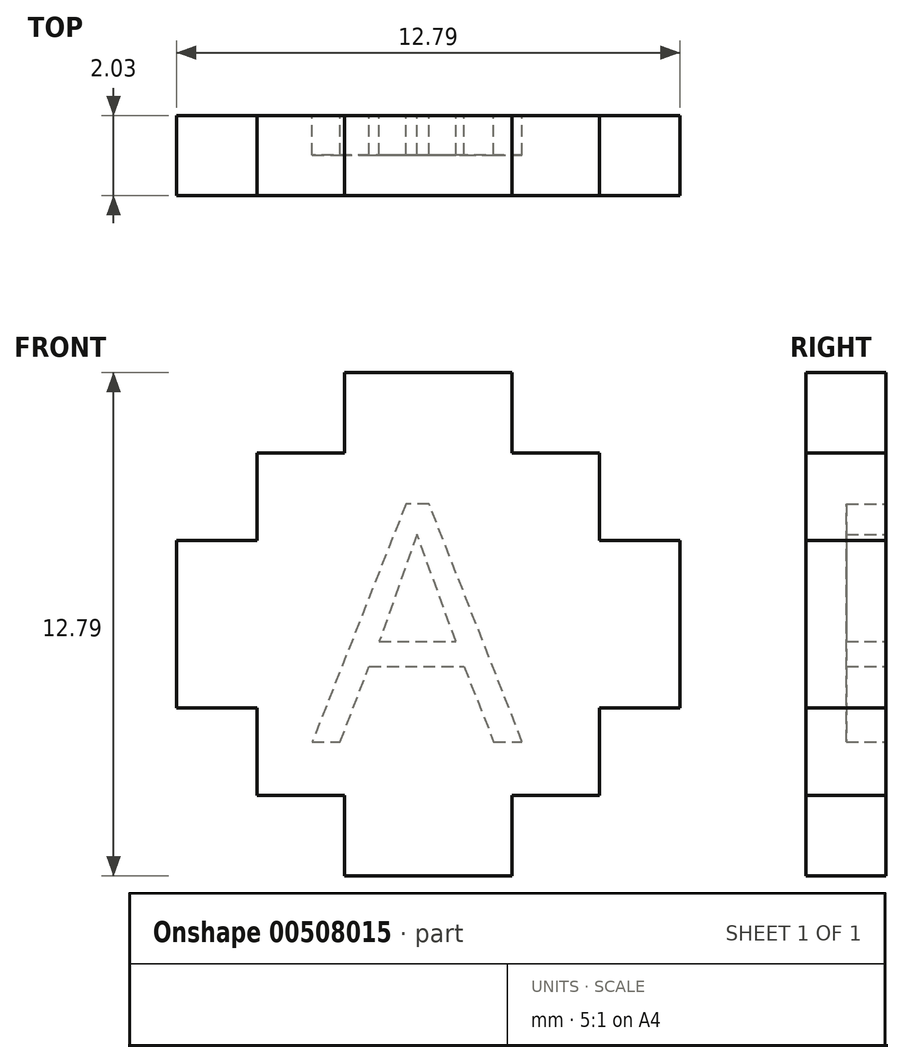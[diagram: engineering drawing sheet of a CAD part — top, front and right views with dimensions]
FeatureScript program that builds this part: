
annotation { "Feature Type Name" : "Feature", "Feature Type Description" : "" }
export const myFeature = defineFeature(function(context is Context, id is Id, definition is map)
    precondition{}
    {
        {
            var Q0;
            Q0=qCreatedBy(makeId("Front.planeOp"),FACE);
            var sketch = newSketch(context, id + "F0", { "sketchPlane" : qUnion([Q0])});
            skLineSegment(sketch, "E0", {"start": v(-17.35, 36.23) * mm, "end": v(-15.22, 36.23) * mm});
            skLineSegment(sketch, "E1", {"start": v(-15.22, 36.23) * mm, "end": v(-15.22, 34.18) * mm});
            skLineSegment(sketch, "E2", {"start": v(-15.22, 34.18) * mm, "end": v(-13, 34.18) * mm});
            skLineSegment(sketch, "E3", {"start": v(-13, 34.18) * mm, "end": v(-13, 31.96) * mm});
            skLineSegment(sketch, "E4", {"start": v(-13, 31.96) * mm, "end": v(-10.95, 31.96) * mm});
            skLineSegment(sketch, "E5", {"start": v(-10.95, 31.96) * mm, "end": v(-10.95, 29.83) * mm});
            skLineSegment(sketch, "E6", {"start": v(-17.35, 36.23) * mm, "end": v(-17.35, 28.94) * mm, "construction": true});
            skLineSegment(sketch, "E7.MirrorCS", {"start": v(-17.35, 36.23) * mm, "end": v(-19.48, 36.23) * mm});
            skLineSegment(sketch, "E8.MirrorCS", {"start": v(-19.48, 36.23) * mm, "end": v(-19.48, 34.18) * mm});
            skLineSegment(sketch, "E9.MirrorCS", {"start": v(-19.48, 34.18) * mm, "end": v(-21.7, 34.18) * mm});
            skLineSegment(sketch, "E10.MirrorCS", {"start": v(-21.7, 34.18) * mm, "end": v(-21.7, 31.96) * mm});
            skLineSegment(sketch, "E11.MirrorCS", {"start": v(-21.7, 31.96) * mm, "end": v(-23.74, 31.96) * mm});
            skLineSegment(sketch, "E12.MirrorCS", {"start": v(-23.74, 31.96) * mm, "end": v(-23.74, 29.83) * mm});
            skLineSegment(sketch, "E13", {"start": v(-23.74, 29.83) * mm, "end": v(-10.95, 29.83) * mm, "construction": true});
            skLineSegment(sketch, "E14.MirrorCS", {"start": v(-23.74, 27.7) * mm, "end": v(-23.74, 29.83) * mm});
            skLineSegment(sketch, "E15.MirrorCS", {"start": v(-21.7, 27.7) * mm, "end": v(-23.74, 27.7) * mm});
            skLineSegment(sketch, "E16.MirrorCS", {"start": v(-21.7, 25.48) * mm, "end": v(-21.7, 27.7) * mm});
            skLineSegment(sketch, "E17.MirrorCS", {"start": v(-19.48, 25.48) * mm, "end": v(-21.7, 25.48) * mm});
            skLineSegment(sketch, "E18.MirrorCS", {"start": v(-19.48, 23.44) * mm, "end": v(-19.48, 25.48) * mm});
            skLineSegment(sketch, "E19.MirrorCS", {"start": v(-17.35, 23.44) * mm, "end": v(-19.48, 23.44) * mm});
            skLineSegment(sketch, "E20.MirrorCS", {"start": v(-17.35, 23.44) * mm, "end": v(-15.22, 23.44) * mm});
            skLineSegment(sketch, "E21.MirrorCS", {"start": v(-15.22, 23.44) * mm, "end": v(-15.22, 25.48) * mm});
            skLineSegment(sketch, "E22.MirrorCS", {"start": v(-15.22, 25.48) * mm, "end": v(-13, 25.48) * mm});
            skLineSegment(sketch, "E23.MirrorCS", {"start": v(-13, 25.48) * mm, "end": v(-13, 27.7) * mm});
            skLineSegment(sketch, "E24.MirrorCS", {"start": v(-13, 27.7) * mm, "end": v(-10.95, 27.7) * mm});
            skLineSegment(sketch, "E25.MirrorCS", {"start": v(-10.95, 27.7) * mm, "end": v(-10.95, 29.83) * mm});
            skLineSegment(sketch, "E26", {"start": v(-17.63, 32.12) * mm, "end": v(-18.6, 29.4) * mm});
            skLineSegment(sketch, "E27", {"start": v(-18.6, 29.4) * mm, "end": v(-16.64, 29.4) * mm});
            skLineSegment(sketch, "E28", {"start": v(-16.64, 29.4) * mm, "end": v(-17.63, 32.12) * mm});
            skLineSegment(sketch, "E29", {"start": v(-17.91, 32.9) * mm, "end": v(-20.29, 26.85) * mm});
            skLineSegment(sketch, "E30", {"start": v(-20.29, 26.85) * mm, "end": v(-19.58, 26.85) * mm});
            skLineSegment(sketch, "E31", {"start": v(-19.58, 26.85) * mm, "end": v(-18.85, 28.76) * mm});
            skLineSegment(sketch, "E32", {"start": v(-18.85, 28.76) * mm, "end": v(-16.43, 28.76) * mm});
            skLineSegment(sketch, "E33", {"start": v(-16.43, 28.76) * mm, "end": v(-15.68, 26.85) * mm});
            skLineSegment(sketch, "E34", {"start": v(-15.68, 26.85) * mm, "end": v(-14.96, 26.85) * mm});
            skLineSegment(sketch, "E35", {"start": v(-14.96, 26.85) * mm, "end": v(-17.32, 32.89) * mm});
            skLineSegment(sketch, "E36", {"start": v(-17.32, 32.89) * mm, "end": v(-17.91, 32.9) * mm});
            skSolve(sketch);
        }
        {
            var Q0;
            Q0=makeQuery(id+"F0.imprint","IMPRINT",FACE,{"disambiguationData":[TD([[makeQuery(id+"F0.imprint","IMPRINT",EDGE,{"derivedFrom":sQuery(id+"F0.wireOp",EDGE,"E0")}),-1.0]])]});
            var Q1;
            Q1=makeQuery(id+"F0.imprint","IMPRINT",FACE,{"disambiguationData":[TD([[makeQuery(id+"F0.imprint","IMPRINT",EDGE,{"derivedFrom":sQuery(id+"F0.wireOp",EDGE,"b25c118d-44e0-46fb-885b-121db1910a24.sketch_text.stroke-0")}),-1.0]])]});
            var Q2;
            Q2=makeQuery(id+"F0.imprint","IMPRINT",FACE,{"disambiguationData":[TD([[makeQuery(id+"F0.imprint","IMPRINT",EDGE,{"derivedFrom":sQuery(id+"F0.wireOp",EDGE,"b25c118d-44e0-46fb-885b-121db1910a24.sketch_text.stroke-8")}),1.0]])]});
            var Q3;
            Q3=makeQuery(id+"F0.imprint","IMPRINT",FACE,{"disambiguationData":[TD([[makeQuery(id+"F0.imprint","IMPRINT",EDGE,{"derivedFrom":sQuery(id+"F0.wireOp",EDGE,"E26")}),1.0]])]});
            var Q4;
            Q4=makeQuery(id+"F0.imprint","IMPRINT",FACE,{"disambiguationData":[TD([[makeQuery(id+"F0.imprint","IMPRINT",EDGE,{"derivedFrom":sQuery(id+"F0.wireOp",EDGE,"E26")}),-1.0]])]});
            extrude(context, id + "F1", {"entities" : qUnion([Q0, Q1, Q2, Q3, Q4]), "depth" : 2.03 * mm, "offsetDistance" : 25 * mm});
        }
        {
            var Q0;
            Q0=makeQuery(id+"F0.imprint","IMPRINT",FACE,{"disambiguationData":[TD([[makeQuery(id+"F0.imprint","IMPRINT",EDGE,{"derivedFrom":sQuery(id+"F0.wireOp",EDGE,"E26")}),-1.0]])]});
            extrude(context, id + "F2", {"entities" : qUnion([Q0]), "operationType" : NewBodyOperationType.REMOVE, "depth" : 1 * mm, "offsetDistance" : 25 * mm});
        }
    });
